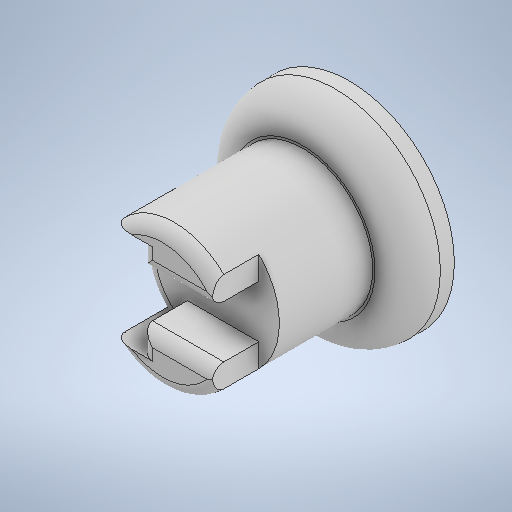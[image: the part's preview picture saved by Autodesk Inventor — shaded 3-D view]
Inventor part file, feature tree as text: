
AUTODESK INVENTOR PART (.ipt)
format: ipt  version: 2025.2 (Build 292293000, 293)  size: 340,480 bytes
history: native  units: in
note: dims shown in document units (in); Inventor stores cm internally (conversion verified against a paired STEP export)
features: extrude x8, sketch x8, fillet x3
ambient origin geometry x8: Origin, YZ Plane, XZ Plane, XY Plane, X Axis, Y Axis, Z Axis, Center Point
bodies: Solid1 (feature_tree)
feature tree (19):
  extrude  "Extrusion1"  Depth=0.5in TaperAngle=0.0deg
  extrude  "Extrusion2"  Depth=0.25in TaperAngle=0.0deg
  extrude  "Extrusion3"  Depth=0.25in TaperAngle=0.0deg
  sketch  "Sketch4"  dims[d9=1.5in d10=0.25in d11=0.0in]
  sketch  "Sketch5"  dims[d12=1.0in d13=0.0in d17=0.5in d18=0.0in]
  extrude  "Extrusion4"  Depth=0.25in TaperAngle=0.0deg
  extrude  "Extrusion5"  Depth=0.5in TaperAngle=0.0deg
  extrude  "Extrusion6"  Depth=0.25in TaperAngle=0.0deg
  fillet  "Fillet1"  Radius=0.25in
  extrude  "Extrusion7"  Depth=0.125in
  extrude  "Extrusion8"  [1 undecoded]
  fillet  "Fillet2"  [1 undecoded]
  fillet  "Fillet3"  [1 undecoded]
  sketch  "Sketch1"  dims[d0=2.25in d1=0.5in d2=0.0in]
  sketch  "Sketch2"  dims[d3=1.8in d4=0.25in d5=0.0in]
  sketch  "Sketch3"  dims[d6=0.85in d7=0.25in d8=0.0in]
  sketch  "Sketch6"  dims[d19=0.17in d20=0.25in d21=0.0in d22=0.25in d23=0.0in]
  sketch  "Sketch7"  dims[d24=0.35in d25=0.125in]
  sketch  "Sketch8"
note: 3 required parameter values undecoded (feature->parameter linkage not recoverable at this tier; creation-order binding heuristic only, values carry confidence <= 0.55)
